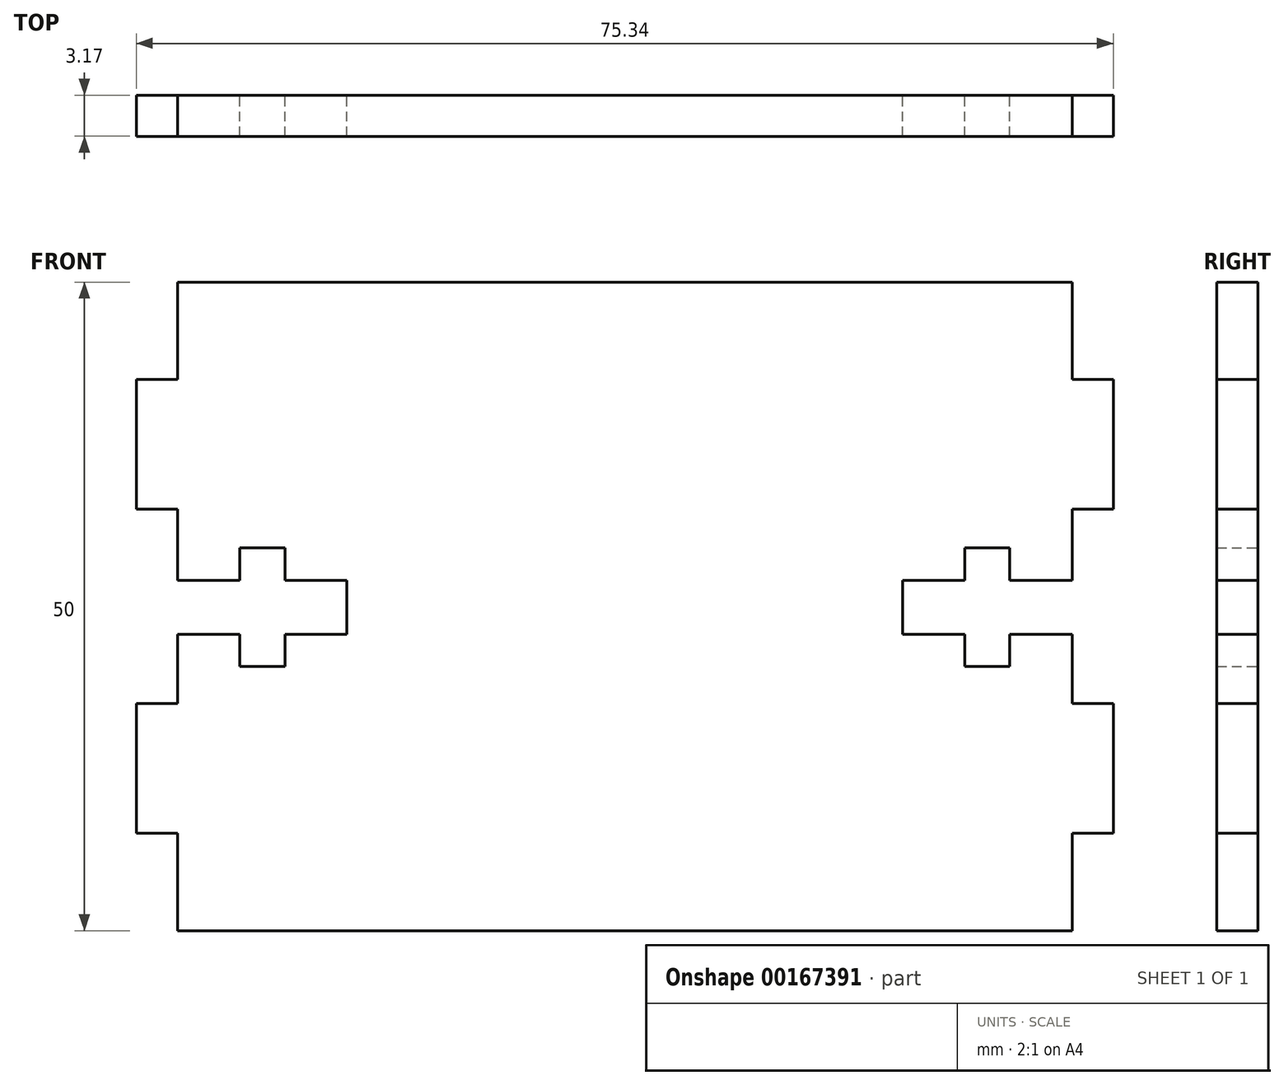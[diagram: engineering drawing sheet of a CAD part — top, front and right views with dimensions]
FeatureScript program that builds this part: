
annotation { "Feature Type Name" : "Feature", "Feature Type Description" : "" }
export const myFeature = defineFeature(function(context is Context, id is Id, definition is map)
    precondition{}
    {
        {
            var Q0;
            Q0=qCreatedBy(makeId("Front.planeOp"),FACE);
            var sketch = newSketch(context, id + "F0", { "sketchPlane" : qUnion([Q0])});
            skLineSegment(sketch, "E0.bottom", {"start": v(-34.5, 25) * mm, "end": v(34.5, 25) * mm});
            skLineSegment(sketch, "E0.top", {"start": v(-34.5, -25) * mm, "end": v(34.5, -25) * mm});
            skLineSegment(sketch, "E0.left", {"start": v(-34.5, 25) * mm, "end": v(-34.5, 17.5) * mm});
            skLineSegment(sketch, "E0.right", {"start": v(34.5, 25) * mm, "end": v(34.5, 17.5) * mm});
            skPoint(sketch, "E0.middle", {"position": v(0, 0) * mm});
            skLineSegment(sketch, "E1.bottom", {"start": v(21.44, 2.01) * mm, "end": v(26.21, 2.01) * mm});
            skLineSegment(sketch, "E1.top", {"start": v(21.44, -2.15) * mm, "end": v(26.21, -2.15) * mm});
            skLineSegment(sketch, "E1.left", {"start": v(21.44, 2.01) * mm, "end": v(21.44, -2.15) * mm});
            skLineSegment(sketch, "E2.bottom", {"start": v(29.7, 4.5) * mm, "end": v(26.21, 4.5) * mm});
            skLineSegment(sketch, "E2.top", {"start": v(29.7, -4.64) * mm, "end": v(26.21, -4.64) * mm});
            skLineSegment(sketch, "E2.left", {"start": v(29.7, 4.5) * mm, "end": v(29.7, 2.01) * mm});
            skLineSegment(sketch, "E2.right", {"start": v(26.21, 4.5) * mm, "end": v(26.21, 2.01) * mm});
            skLineSegment(sketch, "E3.trimOffspring", {"start": v(26.21, -2.15) * mm, "end": v(26.21, -4.64) * mm});
            skLineSegment(sketch, "E4.trimOffspring", {"start": v(29.7, -2.15) * mm, "end": v(29.7, -4.64) * mm});
            skLineSegment(sketch, "E5.trimOffspring", {"start": v(29.7, -2.15) * mm, "end": v(31.32, -2.15) * mm});
            skLineSegment(sketch, "E6.trimOffspring", {"start": v(29.7, 2.01) * mm, "end": v(31.32, 2.01) * mm});
            skLineSegment(sketch, "E7", {"start": v(31.32, -2.15) * mm, "end": v(34.5, -2.15) * mm});
            skLineSegment(sketch, "E8", {"start": v(31.32, 2.01) * mm, "end": v(34.5, 2.01) * mm});
            skLineSegment(sketch, "E9.trimOffspring", {"start": v(34.5, -2.15) * mm, "end": v(34.5, -7.5) * mm});
            skLineSegment(sketch, "E10.bottom", {"start": v(34.5, -7.5) * mm, "end": v(37.67, -7.5) * mm});
            skLineSegment(sketch, "E10.top", {"start": v(34.5, -17.5) * mm, "end": v(37.67, -17.5) * mm});
            skLineSegment(sketch, "E10.right", {"start": v(37.67, -7.5) * mm, "end": v(37.67, -17.5) * mm});
            skLineSegment(sketch, "E11.trimOffspring", {"start": v(34.5, -17.5) * mm, "end": v(34.5, -25) * mm});
            skLineSegment(sketch, "E12.MirrorCS", {"start": v(34.5, 17.5) * mm, "end": v(37.67, 17.5) * mm});
            skLineSegment(sketch, "E13.MirrorCS", {"start": v(37.67, 7.5) * mm, "end": v(37.67, 17.5) * mm});
            skLineSegment(sketch, "E14.MirrorCS", {"start": v(34.5, 7.5) * mm, "end": v(37.67, 7.5) * mm});
            skLineSegment(sketch, "E15.trimOffspring", {"start": v(34.5, 7.5) * mm, "end": v(34.5, 2.01) * mm});
            skLineSegment(sketch, "E16.MirrorCS", {"start": v(-34.5, -7.5) * mm, "end": v(-37.67, -7.5) * mm});
            skLineSegment(sketch, "E17.MirrorCS", {"start": v(-29.7, -2.15) * mm, "end": v(-31.32, -2.15) * mm});
            skLineSegment(sketch, "E18.MirrorCS", {"start": v(-34.5, 17.5) * mm, "end": v(-37.67, 17.5) * mm});
            skLineSegment(sketch, "E19.MirrorCS", {"start": v(-34.5, -17.5) * mm, "end": v(-37.67, -17.5) * mm});
            skLineSegment(sketch, "E20.MirrorCS", {"start": v(-26.21, -2.15) * mm, "end": v(-26.21, -4.64) * mm});
            skLineSegment(sketch, "E21.MirrorCS", {"start": v(-29.7, 2.01) * mm, "end": v(-31.32, 2.01) * mm});
            skLineSegment(sketch, "E22.MirrorCS", {"start": v(-29.7, -2.15) * mm, "end": v(-29.7, -4.64) * mm});
            skLineSegment(sketch, "E23.MirrorCS", {"start": v(-29.7, 4.5) * mm, "end": v(-29.7, 2.01) * mm});
            skLineSegment(sketch, "E24.MirrorCS", {"start": v(-26.21, 4.5) * mm, "end": v(-26.21, 2.01) * mm});
            skLineSegment(sketch, "E25.MirrorCS", {"start": v(-34.5, 7.5) * mm, "end": v(-37.67, 7.5) * mm});
            skLineSegment(sketch, "E26.MirrorCS", {"start": v(-34.5, -2.15) * mm, "end": v(-34.5, -7.5) * mm});
            skLineSegment(sketch, "E27.MirrorCS", {"start": v(-31.32, 2.01) * mm, "end": v(-34.5, 2.01) * mm});
            skLineSegment(sketch, "E28.MirrorCS", {"start": v(-37.67, -7.5) * mm, "end": v(-37.67, -17.5) * mm});
            skLineSegment(sketch, "E29.MirrorCS", {"start": v(-29.7, -4.64) * mm, "end": v(-26.21, -4.64) * mm});
            skLineSegment(sketch, "E30.MirrorCS", {"start": v(-31.32, -2.15) * mm, "end": v(-34.5, -2.15) * mm});
            skLineSegment(sketch, "E31.MirrorCS", {"start": v(-37.67, 7.5) * mm, "end": v(-37.67, 17.5) * mm});
            skLineSegment(sketch, "E32.MirrorCS", {"start": v(-29.7, 4.5) * mm, "end": v(-26.21, 4.5) * mm});
            skLineSegment(sketch, "E33.MirrorCS", {"start": v(-21.44, 2.01) * mm, "end": v(-26.21, 2.01) * mm});
            skLineSegment(sketch, "E34.MirrorCS", {"start": v(-21.44, 2.01) * mm, "end": v(-21.44, -2.15) * mm});
            skLineSegment(sketch, "E35.MirrorCS", {"start": v(-34.5, 7.5) * mm, "end": v(-34.5, 2.01) * mm});
            skLineSegment(sketch, "E36.MirrorCS", {"start": v(-21.44, -2.15) * mm, "end": v(-26.21, -2.15) * mm});
            skLineSegment(sketch, "E37.trimOffspring", {"start": v(-34.5, -17.5) * mm, "end": v(-34.5, -25) * mm});
            skSolve(sketch);
        }
        {
            var Q0;
            Q0 = qSketchRegion(id + "F0", true);
            extrude(context, id + "F1", {"entities" : qUnion([Q0]), "depth" : 3.17 * mm});
        }
    });
